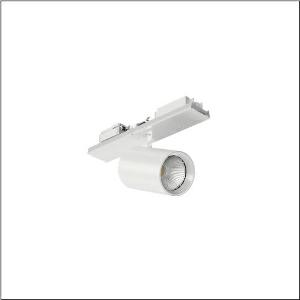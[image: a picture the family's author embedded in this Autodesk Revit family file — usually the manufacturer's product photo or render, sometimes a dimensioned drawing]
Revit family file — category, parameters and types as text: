
# Revit family: licross_r__spot_31_51sl137a43b_0799
name_source: partatom
category: Lighting Fixtures
units: mm (PartAtom-declared; Revit-internal decimal feet)

## family parameters
Cut with Voids When Loaded = No
Host = Face
Light Source = No
Part Type = Normal
Room Calculation Point = No
Round Connector Dimension = Use Diameter
Shared = No

## types (1)
- --- (1 x LED, 3680 lm, 28 W, 4000K)
    Apparent Load = 28 VA
    CIE Flux Codes = 92 97 99 100 100
    Color Rendering = 90
    Color Temperature = 4000K
    Default Elevation = 1800 mm
    Description = Licross® Spot 31, directional spotlight, light control with lens, of plastic, LED rated luminous flux: 3.680lm, light colour: 940, with plug, 3-pole, with phase selection, mains connection: 220..240V, AC, 50/60Hz, of aluminium, traffic white (RAL 9016), length: 140mm, diameter: 90mm, protection rating (complete): IP20, insulation class (complete): insulation class I (protective earthing), certification: CE, packaging unit: 1 piece
    Height = 175 mm
    Lamp = 1 x LED
    Lamp Light Flux = 3680 lm
    Lamp Power = 28 W
    Lamp count = 1
    Length = 90 mm
    Luminous efficacy = 131 lm/W
    Manufacturer = Siteco
    ModVariant = No
    Model = 51SL137A43B
    Mounting Place = Ceiling
    Mounting Type = Pendant
    Number of Poles = 1
    OnlyDefault = Yes
    Power Factor = 1
    Product Name = Licross® Spot 31
    Product group = directional spotlight
    ProductGroupID = 905
    Protection Class = Protection class I
    Protection Degree = IP 20
    RLX_Detail_Level = 1
    RLX_Emergency_Light_Flux = 0 lm
    RLX_Emergency_Type = 0
    RLX_Emergency_Type_DB = No
    RlxData = <blob elided: 14885 chars, md5=2f872cd2>
    Socket = socket
    Standby Power = 0 W
    System Light Flux = 3680 lm
    System Power = 28 W
    Type Comments = factory setting: luminous flux: 100 % | (ON | ON | ON) | 700 mA
    Type Image = l_1245720.jpg
    URL = http://relux.com
    VarID = @adj_063927
    Voltage = 0 V
    Weight = 0.00 kg
    Width = 0 mm  [stored 0 ft]

note: [stored X ft] marks values corroborated as IEEE doubles in the binary element streams (Revit-internal decimal feet)

## geometry (parser evidence)
native form markers: Sweep x11
no freeform markers — native parametric forms only
